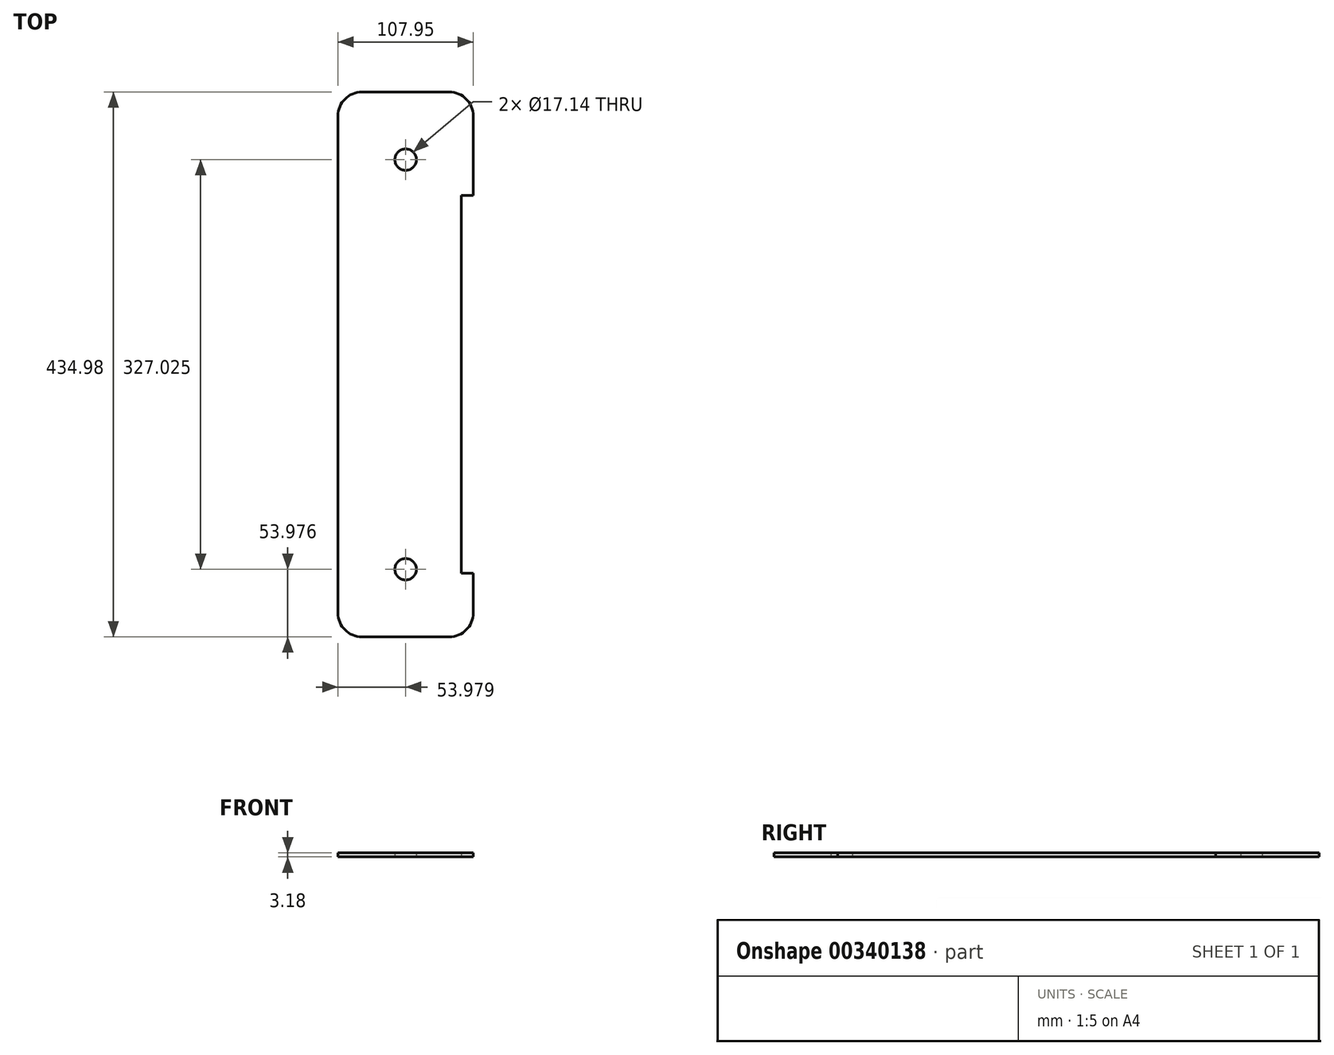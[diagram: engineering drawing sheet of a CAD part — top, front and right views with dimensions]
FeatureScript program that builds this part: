
annotation { "Feature Type Name" : "Feature", "Feature Type Description" : "" }
export const myFeature = defineFeature(function(context is Context, id is Id, definition is map)
    precondition{}
    {
        {
            var Q0;
            Q0=qCreatedBy(makeId("Top.planeOp"),FACE);
            var sketch = newSketch(context, id + "F0", { "sketchPlane" : qUnion([Q0])});
            skLineSegment(sketch, "E0.bottom", {"start": v(-130.08, 214.6) * mm, "end": v(-22.13, 214.6) * mm});
            skLineSegment(sketch, "E0.top", {"start": v(-130.08, -220.38) * mm, "end": v(-22.13, -220.38) * mm});
            skLineSegment(sketch, "E0.left", {"start": v(-130.08, 214.6) * mm, "end": v(-130.08, -220.38) * mm});
            skLineSegment(sketch, "E0.right", {"start": v(-22.13, 214.6) * mm, "end": v(-22.13, 132.05) * mm});
            skLineSegment(sketch, "E1", {"start": v(-22.13, 132.05) * mm, "end": v(-31.65, 132.05) * mm});
            skLineSegment(sketch, "E2", {"start": v(-31.65, 132.05) * mm, "end": v(-31.65, -169.58) * mm});
            skLineSegment(sketch, "E3", {"start": v(-31.65, -169.58) * mm, "end": v(-22.13, -169.58) * mm});
            skLineSegment(sketch, "E4.trimOffspring", {"start": v(-22.13, -169.58) * mm, "end": v(-22.13, -220.38) * mm});
            skPoint(sketch, "E5", {"position": v(-76.1, -220.38) * mm});
            skCircle(sketch, "E6", {"center": v(-76.1, -166.4) * mm, "radius": 8.57 * mm});
            skLineSegment(sketch, "E7", {"start": v(-130.08, 214.6) * mm, "end": v(-130.08, 160.62) * mm, "construction": true});
            skLineSegment(sketch, "E8", {"start": v(-130.08, -220.38) * mm, "end": v(-130.08, -166.4) * mm, "construction": true});
            skCircle(sketch, "E9", {"center": v(-76.1, 160.62) * mm, "radius": 8.57 * mm});
            skPoint(sketch, "E9.centerSnap0", {"position": v(-76.1, 214.6) * mm});
            skSolve(sketch);
        }
        {
            var Q0;
            Q0 = qSketchRegion(id + "F0", true);
            extrude(context, id + "F1", {"entities" : qUnion([Q0]), "depth" : 3.17 * mm});
        }
        {
            var Q0;
            Q0=makeQuery(id+"F1.opExtrude","SWEPT_EDGE",EDGE,{"disambiguationData":[OSD([sQuery(id+"F0.wireOp",EDGE,"E0.top"),sQuery(id+"F0.wireOp",EDGE,"E0.left")])]});
            var Q1;
            Q1=makeQuery(id+"F1.opExtrude","SWEPT_EDGE",EDGE,{"disambiguationData":[OSD([sQuery(id+"F0.wireOp",EDGE,"E0.top"),sQuery(id+"F0.wireOp",EDGE,"E4.trimOffspring")])]});
            var Q2;
            Q2=makeQuery(id+"F1.opExtrude","SWEPT_EDGE",EDGE,{"disambiguationData":[OSD([sQuery(id+"F0.wireOp",EDGE,"E0.bottom"),sQuery(id+"F0.wireOp",EDGE,"E0.left")])]});
            var Q3;
            Q3=makeQuery(id+"F1.opExtrude","SWEPT_EDGE",EDGE,{"disambiguationData":[OSD([sQuery(id+"F0.wireOp",EDGE,"E0.top"),sQuery(id+"F0.wireOp",EDGE,"E0.left")])]});
            var Q4;
            Q4=makeQuery(id+"F1.opExtrude","SWEPT_EDGE",EDGE,{"disambiguationData":[OSD([sQuery(id+"F0.wireOp",EDGE,"E0.bottom"),sQuery(id+"F0.wireOp",EDGE,"E0.right")])]});
            fillet(context, id + "F2", {"entities" : qUnion([Q0, Q1, Q2, Q3, Q4]), "radius" : 19.05 * mm, "tangentPropagation" : true, "allowEdgeOverflow" : false});
        }
    });
